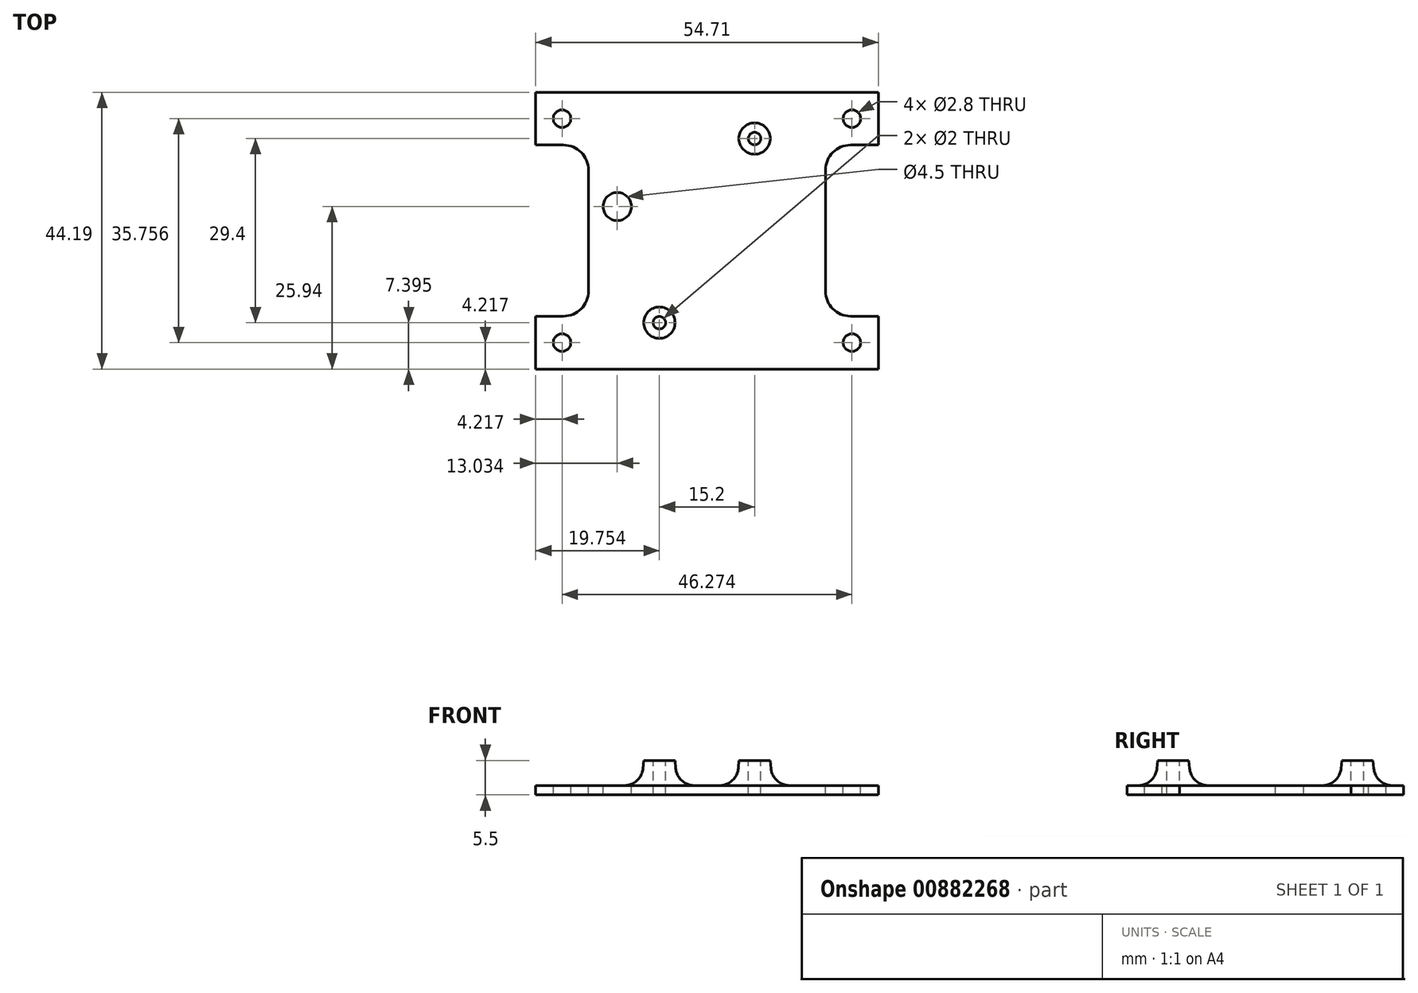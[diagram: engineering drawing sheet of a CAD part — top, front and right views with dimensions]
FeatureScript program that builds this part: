
annotation { "Feature Type Name" : "Feature", "Feature Type Description" : "" }
export const myFeature = defineFeature(function(context is Context, id is Id, definition is map)
    precondition{}
    {
        {
            var Q0;
            Q0=qCreatedBy(makeId("Top.planeOp"),FACE);
            var sketch = newSketch(context, id + "F0", { "sketchPlane" : qUnion([Q0])});
            skLineSegment(sketch, "E0.bottom", {"start": v(0, 0) * mm, "end": v(51.3, 0) * mm});
            skLineSegment(sketch, "E0.top", {"start": v(0, 74) * mm, "end": v(51.3, 74) * mm});
            skLineSegment(sketch, "E0.left", {"start": v(0, 0) * mm, "end": v(0, 74) * mm});
            skLineSegment(sketch, "E0.right", {"start": v(51.3, 0) * mm, "end": v(51.3, 74) * mm});
            skLineSegment(sketch, "E1.bottom", {"start": v(0, 69) * mm, "end": v(16.7, 69) * mm, "construction": true});
            skLineSegment(sketch, "E1.top", {"start": v(0, 55) * mm, "end": v(16.7, 55) * mm, "construction": true});
            skLineSegment(sketch, "E1.left", {"start": v(0, 69) * mm, "end": v(0, 55) * mm, "construction": true});
            skLineSegment(sketch, "E1.right", {"start": v(16.7, 69) * mm, "end": v(16.7, 55) * mm, "construction": true});
            skLineSegment(sketch, "E2.bottom", {"start": v(0, 33) * mm, "end": v(16.7, 33) * mm, "construction": true});
            skLineSegment(sketch, "E2.top", {"start": v(0, 19) * mm, "end": v(16.7, 19) * mm, "construction": true});
            skLineSegment(sketch, "E2.left", {"start": v(0, 33) * mm, "end": v(0, 19) * mm, "construction": true});
            skLineSegment(sketch, "E2.right", {"start": v(16.7, 33) * mm, "end": v(16.7, 19) * mm, "construction": true});
            skLineSegment(sketch, "E3.bottom", {"start": v(51.3, 69) * mm, "end": v(34.6, 69) * mm, "construction": true});
            skLineSegment(sketch, "E3.top", {"start": v(51.3, 55) * mm, "end": v(34.6, 55) * mm, "construction": true});
            skLineSegment(sketch, "E3.left", {"start": v(51.3, 69) * mm, "end": v(51.3, 55) * mm, "construction": true});
            skLineSegment(sketch, "E3.right", {"start": v(34.6, 69) * mm, "end": v(34.6, 55) * mm, "construction": true});
            skLineSegment(sketch, "E4.bottom", {"start": v(51.3, 33) * mm, "end": v(34.6, 33) * mm, "construction": true});
            skLineSegment(sketch, "E4.top", {"start": v(51.3, 19) * mm, "end": v(34.6, 19) * mm, "construction": true});
            skLineSegment(sketch, "E4.left", {"start": v(51.3, 33) * mm, "end": v(51.3, 19) * mm, "construction": true});
            skLineSegment(sketch, "E4.right", {"start": v(34.6, 33) * mm, "end": v(34.6, 19) * mm, "construction": true});
            skCircle(sketch, "E5", {"center": v(11.21, 3.92) * mm, "radius": 1.6 * mm});
            skCircle(sketch, "E6", {"center": v(32.51, 3.92) * mm, "radius": 1.6 * mm});
            skCircle(sketch, "E7", {"center": v(49.43, 3.92) * mm, "radius": 1.6 * mm});
            skCircle(sketch, "E8", {"center": v(49.43, 72.12) * mm, "radius": 1.6 * mm});
            skCircle(sketch, "E9", {"center": v(1.88, 72.12) * mm, "radius": 1.6 * mm});
            skLineSegment(sketch, "E10", {"start": v(1.88, 72.12) * mm, "end": v(49.43, 72.12) * mm, "construction": true});
            skSolve(sketch);
        }
        {
            var Q0;
            {var subQ10=sQuery(id+"F0.wireOp",EDGE,"E0.bottom");Q0=makeQuery(id+"F0.imprint","IMPRINT",FACE,{"disambiguationData":[TD([[makeQuery(id+"F0.imprint","IMPRINT",EDGE,{"derivedFrom":subQ10}),1.0]])]});}
            var sketch = newSketch(context, id + "F1", { "sketchPlane" : qUnion([Q0])});
            skLineSegment(sketch, "E11.0", {"start": v(-1.7, -1.7) * mm, "end": v(-1.7, 75.7) * mm});
            skLineSegment(sketch, "E11.1", {"start": v(-1.7, -1.7) * mm, "end": v(53, -1.7) * mm});
            skLineSegment(sketch, "E11.2", {"start": v(53, -1.7) * mm, "end": v(53, 75.7) * mm});
            skLineSegment(sketch, "E11.3", {"start": v(-1.7, 75.7) * mm, "end": v(53, 75.7) * mm});
            skSolve(sketch);
        }
        {
            var Q0;
            Q0=qSketchRegion(id+"F1",true);
            extrude(context, id + "F2", {"entities" : qUnion([Q0]), "depth" : 1.5 * mm, "offsetDistance" : 25 * mm});
        }
        {
            var Q0;
            {var subQ0=sQuery(id+"F6GXzuOHntquvKr_1.wireOp",EDGE,"s17BW498-6bKE-bvLq-Xut5-QpTvFKj44F6L");var subQ1=sQuery(id+"F6GXzuOHntquvKr_1.wireOp",EDGE,"KkH5eE3K-AXJX-ZvZF-UOav-HisGAflkKzs7");var subQ2=sQuery(id+"F6GXzuOHntquvKr_1.wireOp",EDGE,"Lc9ymual-iNm1-0gbj-nJ7k-jOShu6Us2LTm");var subQ3=sQuery(id+"F6GXzuOHntquvKr_1.wireOp",EDGE,"rWmqq6mH-Y7ee-QEVy-FZAS-sSJdcVXWXRMh");var subQ4=sQuery(id+"F6GXzuOHntquvKr_1.wireOp",EDGE,"c878682a-a3fc-495e-9975-6ad3af1e72822.MirrorCS");var subQ5=sQuery(id+"F6GXzuOHntquvKr_1.wireOp",EDGE,"c878682a-a3fc-495e-9975-6ad3af1e72821.MirrorCS");var subQ6=sQuery(id+"F6GXzuOHntquvKr_1.wireOp",EDGE,"c878682a-a3fc-495e-9975-6ad3af1e72820.MirrorCS");var subQ7=sQuery(id+"F6GXzuOHntquvKr_1.wireOp",EDGE,"gumsQsr6-K8Im-hkzl-JbXD-zjOCVHvVJb9f");var subQ8=sQuery(id+"F6GXzuOHntquvKr_1.wireOp",EDGE,"ybwg6MaK-QAga-Fhxh-U395-XssyxfBwCAxj");var subQ9=sQuery(id+"F6GXzuOHntquvKr_1.wireOp",EDGE,"c878682a-a3fc-495e-9975-6ad3af1e72826.MirrorCS");var subQ10=sQuery(id+"F1.wireOp",EDGE,"E11.1");var subQ11=sQuery(id+"F6GXzuOHntquvKr_1.wireOp",EDGE,"JJFlnewm-85mE-duSD-FSQs-iFHrIXV6r2m2");var subQ12=sQuery(id+"F1.wireOp",EDGE,"E11.3");var subQ13=sQuery(id+"F6GXzuOHntquvKr_1.wireOp",EDGE,"c878682a-a3fc-495e-9975-6ad3af1e72823.MirrorCS");var subQ14=sQuery(id+"F1.wireOp",EDGE,"E11.0");var subQ15=sQuery(id+"F6GXzuOHntquvKr_1.wireOp",EDGE,"c878682a-a3fc-495e-9975-6ad3af1e72827.MirrorCS");var subQ16=sQuery(id+"F1.wireOp",EDGE,"E11.2");var subQ17=sQuery(id+"F6GXzuOHntquvKr_1.wireOp",EDGE,"KYmkqSoi-ySKa-ysJT-3wLy-sUcAUlMoE4Lw");var subQ18=sQuery(id+"F6GXzuOHntquvKr_1.wireOp",EDGE,"rGfCT0qz-87yu-6z5P-5utD-09FTJLvzhlS5");var subQ19=sQuery(id+"F6GXzuOHntquvKr_1.wireOp",EDGE,"38AYfzUa-mGmV-3WPU-EBOK-ykPB0kyNFQ41");Q0=makeQuery(id+"F7ymWyKb8andwvf_1.boolean.opBoolean","SPLIT",FACE,{"disambiguationData":[TD([makeQuery(id+"F2.opExtrude","SWEPT_FACE",FACE,{"disambiguationData":[OSD([subQ14])]})])],"derivedFrom":makeQuery(id+"F7FFp2r9aQODMAd_1.boolean.opBoolean","MERGE",FACE,{"derivedFrom":[makeQuery(id+"F2.opExtrude","CAP_FACE",FACE,{"disambiguationData":[OSD([subQ14,subQ10,subQ16,subQ12])],"isStart":false}),makeQuery(id+"F7FFp2r9aQODMAd_1.opExtrude","CAP_FACE",FACE,{"disambiguationData":[OSD([subQ17,subQ1,subQ18,sQuery(id+"F6GXzuOHntquvKr_1.wireOp",EDGE,"2ph3kAtd-Sgn4-jQcT-vLBk-Z36Royi8zWen"),subQ11])],"isStart":false}),makeQuery(id+"F7FFp2r9aQODMAd_1.opExtrude","CAP_FACE",FACE,{"disambiguationData":[OSD([subQ8,subQ19,subQ0,sQuery(id+"F6GXzuOHntquvKr_1.wireOp",EDGE,"SVgNKyan-8M9S-muwL-MN39-nCX4EP7pWvKC"),subQ2])],"isStart":false}),makeQuery(id+"F7FFp2r9aQODMAd_1.opExtrude","CAP_FACE",FACE,{"disambiguationData":[OSD([subQ6,subQ4,sQuery(id+"F6GXzuOHntquvKr_1.wireOp",EDGE,"c878682a-a3fc-495e-9975-6ad3af1e72824.MirrorCS"),subQ15,subQ3])],"isStart":false}),makeQuery(id+"F7FFp2r9aQODMAd_1.opExtrude","CAP_FACE",FACE,{"disambiguationData":[OSD([subQ5,subQ13,sQuery(id+"F6GXzuOHntquvKr_1.wireOp",EDGE,"c878682a-a3fc-495e-9975-6ad3af1e72825.MirrorCS"),subQ9,subQ7])],"isStart":false})]})});}
            var sketch = newSketch(context, id + "F3", { "sketchPlane" : qUnion([Q0])});
            skLineSegment(sketch, "E12.bottom", {"start": v(6.73, 8.81) * mm, "end": v(44.57, 8.81) * mm, "construction": true});
            skLineSegment(sketch, "E12.top", {"start": v(6.73, 69) * mm, "end": v(44.57, 69) * mm, "construction": true});
            skLineSegment(sketch, "E12.left", {"start": v(6.73, 8.8) * mm, "end": v(6.73, 69) * mm, "construction": true});
            skLineSegment(sketch, "E12.right", {"start": v(44.57, 8.81) * mm, "end": v(44.57, 69) * mm, "construction": true});
            skLineSegment(sketch, "E13", {"start": v(6.73, 38.9) * mm, "end": v(44.57, 38.9) * mm, "construction": true});
            skLineSegment(sketch, "E14", {"start": v(25.65, 8.81) * mm, "end": v(25.65, 69) * mm, "construction": true});
            skLineSegment(sketch, "E15.bottom", {"start": v(6.73, 16.8) * mm, "end": v(-1.7, 16.8) * mm});
            skLineSegment(sketch, "E15.top", {"start": v(6.73, 25.24) * mm, "end": v(-1.7, 25.24) * mm});
            skLineSegment(sketch, "E16.MirrorCS", {"start": v(44.57, 25.24) * mm, "end": v(53, 25.24) * mm});
            skLineSegment(sketch, "E17.MirrorCS", {"start": v(44.57, 16.81) * mm, "end": v(53, 16.81) * mm});
            skLineSegment(sketch, "E18.MirrorCS", {"start": v(6.73, 61) * mm, "end": v(-1.7, 61) * mm});
            skLineSegment(sketch, "E19.MirrorCS", {"start": v(44.57, 61) * mm, "end": v(53, 61) * mm});
            skLineSegment(sketch, "E20.MirrorCS", {"start": v(44.57, 52.57) * mm, "end": v(53, 52.57) * mm});
            skLineSegment(sketch, "E21.MirrorCS", {"start": v(6.73, 52.57) * mm, "end": v(-1.7, 52.57) * mm});
            skCircle(sketch, "E22", {"center": v(2.52, 21.03) * mm, "radius": 1.4 * mm});
            skPoint(sketch, "E22.centerSnap1", {"position": v(-1.7, 21.03) * mm});
            skCircle(sketch, "E23.MirrorC", {"center": v(48.8, 21.03) * mm, "radius": 1.4 * mm});
            skCircle(sketch, "E24.MirrorC", {"center": v(48.8, 56.78) * mm, "radius": 1.4 * mm});
            skCircle(sketch, "E25.MirrorC", {"center": v(2.52, 56.78) * mm, "radius": 1.4 * mm});
            skLineSegment(sketch, "E26.bottom", {"start": v(15.55, 60.6) * mm, "end": v(35.75, 60.6) * mm, "construction": true});
            skLineSegment(sketch, "E26.top", {"start": v(15.55, 17.2) * mm, "end": v(35.75, 17.2) * mm, "construction": true});
            skLineSegment(sketch, "E26.left", {"start": v(15.55, 60.6) * mm, "end": v(15.55, 17.2) * mm, "construction": true});
            skLineSegment(sketch, "E26.right", {"start": v(35.75, 60.6) * mm, "end": v(35.75, 17.2) * mm, "construction": true});
            skLineSegment(sketch, "E27", {"start": v(2.52, 56.78) * mm, "end": v(48.8, 56.78) * mm, "construction": true});
            skLineSegment(sketch, "E28", {"start": v(48.8, 56.78) * mm, "end": v(48.8, 21.03) * mm, "construction": true});
            skLineSegment(sketch, "E29", {"start": v(48.8, 21.03) * mm, "end": v(2.52, 21.03) * mm, "construction": true});
            skLineSegment(sketch, "E30", {"start": v(2.52, 21.03) * mm, "end": v(2.52, 56.78) * mm, "construction": true});
            skLineSegment(sketch, "E31", {"start": v(6.73, 61) * mm, "end": v(44.57, 61) * mm});
            skLineSegment(sketch, "E32", {"start": v(6.73, 16.8) * mm, "end": v(44.57, 16.81) * mm});
            skLineSegment(sketch, "E33", {"start": v(6.73, 52.57) * mm, "end": v(6.73, 25.24) * mm});
            skLineSegment(sketch, "E34", {"start": v(44.57, 52.57) * mm, "end": v(44.57, 25.24) * mm});
            skLineSegment(sketch, "E35", {"start": v(-1.7, 61) * mm, "end": v(-1.7, 75.7) * mm});
            skLineSegment(sketch, "E36", {"start": v(-1.7, 75.7) * mm, "end": v(53, 75.7) * mm});
            skLineSegment(sketch, "E37", {"start": v(53, 75.7) * mm, "end": v(53, 61) * mm});
            skLineSegment(sketch, "E38", {"start": v(53, 52.57) * mm, "end": v(53, 25.24) * mm});
            skLineSegment(sketch, "E39", {"start": v(53, 16.81) * mm, "end": v(53, -1.7) * mm});
            skLineSegment(sketch, "E40", {"start": v(53, -1.7) * mm, "end": v(-1.7, -1.7) * mm});
            skLineSegment(sketch, "E41", {"start": v(-1.7, -1.7) * mm, "end": v(-1.7, 16.8) * mm});
            skLineSegment(sketch, "E42", {"start": v(-1.7, 25.24) * mm, "end": v(-1.7, 52.57) * mm});
            skCircle(sketch, "E43", {"center": v(33.25, 53.6) * mm, "radius": 1 * mm});
            skCircle(sketch, "E44", {"center": v(18.05, 24.2) * mm, "radius": 1 * mm});
            skLineSegment(sketch, "E45", {"start": v(15.55, 38.9) * mm, "end": v(35.75, 38.9) * mm, "construction": true});
            skLineSegment(sketch, "E46", {"start": v(25.65, 60.6) * mm, "end": v(25.65, 17.2) * mm, "construction": true});
            skCircle(sketch, "E47", {"center": v(11.33, 42.75) * mm, "radius": 2.25 * mm});
            skSolve(sketch);
        }
        {
            var Q0;
            Q0=qSketchRegion(id+"F3",true);
            extrude(context, id + "F4", {"entities" : qUnion([Q0]), "operationType" : NewBodyOperationType.REMOVE, "endBound" : BoundingType.THROUGH_ALL, "oppositeDirection" : true, "depth" : 25 * mm, "offsetDistance" : 25 * mm});
        }
        {
            var Q0;
            Q0=makeQuery(id+"F4.boolean.opBoolean","COPY",EDGE,{"derivedFrom":makeQuery(id+"F4.opExtrude","SWEPT_EDGE",EDGE,{"disambiguationData":[OSD([sQuery(id+"F1.wireOp",EDGE,"E11.0"),sQuery(id+"F3.wireOp",EDGE,"E18.MirrorCS"),sQuery(id+"F3.wireOp",EDGE,"E35")])]})});
            var Q1;
            Q1=makeQuery(id+"F4.boolean.opBoolean","COPY",EDGE,{"derivedFrom":makeQuery(id+"F4.opExtrude","SWEPT_EDGE",EDGE,{"disambiguationData":[OSD([sQuery(id+"F1.wireOp",EDGE,"E11.0"),sQuery(id+"F3.wireOp",EDGE,"E21.MirrorCS"),sQuery(id+"F3.wireOp",EDGE,"E42")])]})});
            var Q2;
            Q2=makeQuery(id+"F4.boolean.opBoolean","COPY",EDGE,{"derivedFrom":makeQuery(id+"F4.opExtrude","SWEPT_EDGE",EDGE,{"disambiguationData":[OSD([sQuery(id+"F1.wireOp",EDGE,"E11.0"),sQuery(id+"F3.wireOp",EDGE,"E15.top"),sQuery(id+"F3.wireOp",EDGE,"E42")])]})});
            var Q3;
            Q3=makeQuery(id+"F4.boolean.opBoolean","COPY",EDGE,{"derivedFrom":makeQuery(id+"F4.opExtrude","SWEPT_EDGE",EDGE,{"disambiguationData":[OSD([sQuery(id+"F1.wireOp",EDGE,"E11.0"),sQuery(id+"F3.wireOp",EDGE,"E15.bottom"),sQuery(id+"F3.wireOp",EDGE,"E41")])]})});
            var Q4;
            Q4=makeQuery(id+"F4.boolean.opBoolean","COPY",EDGE,{"derivedFrom":makeQuery(id+"F4.opExtrude","SWEPT_EDGE",EDGE,{"disambiguationData":[OSD([sQuery(id+"F3.wireOp",EDGE,"E15.top"),sQuery(id+"F3.wireOp",EDGE,"E33")])]})});
            var Q5;
            Q5=makeQuery(id+"F4.boolean.opBoolean","COPY",EDGE,{"derivedFrom":makeQuery(id+"F4.opExtrude","SWEPT_EDGE",EDGE,{"disambiguationData":[OSD([sQuery(id+"F3.wireOp",EDGE,"E21.MirrorCS"),sQuery(id+"F3.wireOp",EDGE,"E33")])]})});
            var Q6;
            Q6=makeQuery(id+"F4.boolean.opBoolean","COPY",EDGE,{"derivedFrom":makeQuery(id+"F4.opExtrude","SWEPT_EDGE",EDGE,{"disambiguationData":[OSD([sQuery(id+"F1.wireOp",EDGE,"E11.2"),sQuery(id+"F3.wireOp",EDGE,"E19.MirrorCS"),sQuery(id+"F3.wireOp",EDGE,"E37")])]})});
            var Q7;
            Q7=makeQuery(id+"F4.boolean.opBoolean","COPY",EDGE,{"derivedFrom":makeQuery(id+"F4.opExtrude","SWEPT_EDGE",EDGE,{"disambiguationData":[OSD([sQuery(id+"F1.wireOp",EDGE,"E11.2"),sQuery(id+"F3.wireOp",EDGE,"E20.MirrorCS"),sQuery(id+"F3.wireOp",EDGE,"E38")])]})});
            var Q8;
            Q8=makeQuery(id+"F4.boolean.opBoolean","COPY",EDGE,{"derivedFrom":makeQuery(id+"F4.opExtrude","SWEPT_EDGE",EDGE,{"disambiguationData":[OSD([sQuery(id+"F3.wireOp",EDGE,"E20.MirrorCS"),sQuery(id+"F3.wireOp",EDGE,"E34")])]})});
            var Q9;
            Q9=makeQuery(id+"F4.boolean.opBoolean","COPY",EDGE,{"derivedFrom":makeQuery(id+"F4.opExtrude","SWEPT_EDGE",EDGE,{"disambiguationData":[OSD([sQuery(id+"F3.wireOp",EDGE,"E16.MirrorCS"),sQuery(id+"F3.wireOp",EDGE,"E34")])]})});
            var Q10;
            Q10=makeQuery(id+"F4.boolean.opBoolean","COPY",EDGE,{"derivedFrom":makeQuery(id+"F4.opExtrude","SWEPT_EDGE",EDGE,{"disambiguationData":[OSD([sQuery(id+"F1.wireOp",EDGE,"E11.2"),sQuery(id+"F3.wireOp",EDGE,"E16.MirrorCS"),sQuery(id+"F3.wireOp",EDGE,"E38")])]})});
            var Q11;
            Q11=makeQuery(id+"F4.boolean.opBoolean","COPY",EDGE,{"derivedFrom":makeQuery(id+"F4.opExtrude","SWEPT_EDGE",EDGE,{"disambiguationData":[OSD([sQuery(id+"F1.wireOp",EDGE,"E11.2"),sQuery(id+"F3.wireOp",EDGE,"E17.MirrorCS"),sQuery(id+"F3.wireOp",EDGE,"E39")])]})});
            fillet(context, id + "F5", {"entities" : qUnion([Q0, Q1, Q2, Q3, Q4, Q5, Q6, Q7, Q8, Q9, Q10, Q11]), "radius" : 4 * mm, "tangentPropagation" : true, "allowEdgeOverflow" : false});
        }
        {
            var Q0;
            Q0=makeQuery(id+"F2.opExtrude","CAP_FACE",FACE,{"disambiguationData":[OSD([sQuery(id+"F1.wireOp",EDGE,"E11.0"),sQuery(id+"F1.wireOp",EDGE,"E11.1"),sQuery(id+"F1.wireOp",EDGE,"E11.2"),sQuery(id+"F1.wireOp",EDGE,"E11.3")])],"isStart":false});
            var sketch = newSketch(context, id + "F6", { "sketchPlane" : qUnion([Q0])});
            skCircle(sketch, "E48", {"center": v(18.05, 24.2) * mm, "radius": 3 * mm});
            skCircle(sketch, "E49", {"center": v(33.25, 53.6) * mm, "radius": 3 * mm});
            skCircle(sketch, "E50", {"center": v(18.05, 24.2) * mm, "radius": 1 * mm});
            skCircle(sketch, "E51", {"center": v(33.25, 53.6) * mm, "radius": 1 * mm});
            skSolve(sketch);
        }
        {
            var Q0;
            Q0=qSketchRegion(id+"F6",true);
            extrude(context, id + "F7", {"entities" : qUnion([Q0]), "operationType" : NewBodyOperationType.ADD, "depth" : 4 * mm, "offsetDistance" : 25 * mm});
        }
        {
            var Q0;
            Q0=makeQuery(id+"F7.opExtrude","CAP_EDGE",EDGE,{"disambiguationData":[OSD([sQuery(id+"F6.wireOp",EDGE,"E48")])],"isStart":false});
            var Q1;
            Q1=makeQuery(id+"F7.opExtrude","CAP_EDGE",EDGE,{"disambiguationData":[OSD([sQuery(id+"F6.wireOp",EDGE,"E49")])],"isStart":false});
            chamfer(context, id + "F8", {"entities" : qUnion([Q0, Q1]), "chamferType" : ChamferType.OFFSET_ANGLE, "width" : .5 * mm, "oppositeDirection" : false, "angle" : 85 * degree, "tangentPropagation" : true});
        }
        {
            var Q0;
            Q0=makeQuery(id+"F8.opChamfer","BLEND_EDGE",EDGE,{"blendedFrom":[makeQuery(id+"F7.opExtrude","CAP_EDGE",EDGE,{"disambiguationData":[OSD([sQuery(id+"F6.wireOp",EDGE,"E48")])],"isStart":false}),makeQuery(id+"F2.opExtrude","CAP_FACE",FACE,{"disambiguationData":[OSD([sQuery(id+"F1.wireOp",EDGE,"E11.0"),sQuery(id+"F1.wireOp",EDGE,"E11.1"),sQuery(id+"F1.wireOp",EDGE,"E11.2"),sQuery(id+"F1.wireOp",EDGE,"E11.3")])],"isStart":false})],"blendedInto":[makeQuery(id+"F2.opExtrude","CAP_FACE",FACE,{"disambiguationData":[OSD([sQuery(id+"F1.wireOp",EDGE,"E11.0"),sQuery(id+"F1.wireOp",EDGE,"E11.1"),sQuery(id+"F1.wireOp",EDGE,"E11.2"),sQuery(id+"F1.wireOp",EDGE,"E11.3")])],"isStart":false})]});
            var Q1;
            Q1=makeQuery(id+"F8.opChamfer","BLEND_EDGE",EDGE,{"blendedFrom":[makeQuery(id+"F7.opExtrude","CAP_EDGE",EDGE,{"disambiguationData":[OSD([sQuery(id+"F6.wireOp",EDGE,"E49")])],"isStart":false}),makeQuery(id+"F2.opExtrude","CAP_FACE",FACE,{"disambiguationData":[OSD([sQuery(id+"F1.wireOp",EDGE,"E11.0"),sQuery(id+"F1.wireOp",EDGE,"E11.1"),sQuery(id+"F1.wireOp",EDGE,"E11.2"),sQuery(id+"F1.wireOp",EDGE,"E11.3")])],"isStart":false})],"blendedInto":[makeQuery(id+"F2.opExtrude","CAP_FACE",FACE,{"disambiguationData":[OSD([sQuery(id+"F1.wireOp",EDGE,"E11.0"),sQuery(id+"F1.wireOp",EDGE,"E11.1"),sQuery(id+"F1.wireOp",EDGE,"E11.2"),sQuery(id+"F1.wireOp",EDGE,"E11.3")])],"isStart":false})]});
            fillet(context, id + "F9", {"entities" : qUnion([Q0, Q1]), "radius" : 3 * mm, "tangentPropagation" : true, "allowEdgeOverflow" : false});
        }
    });
